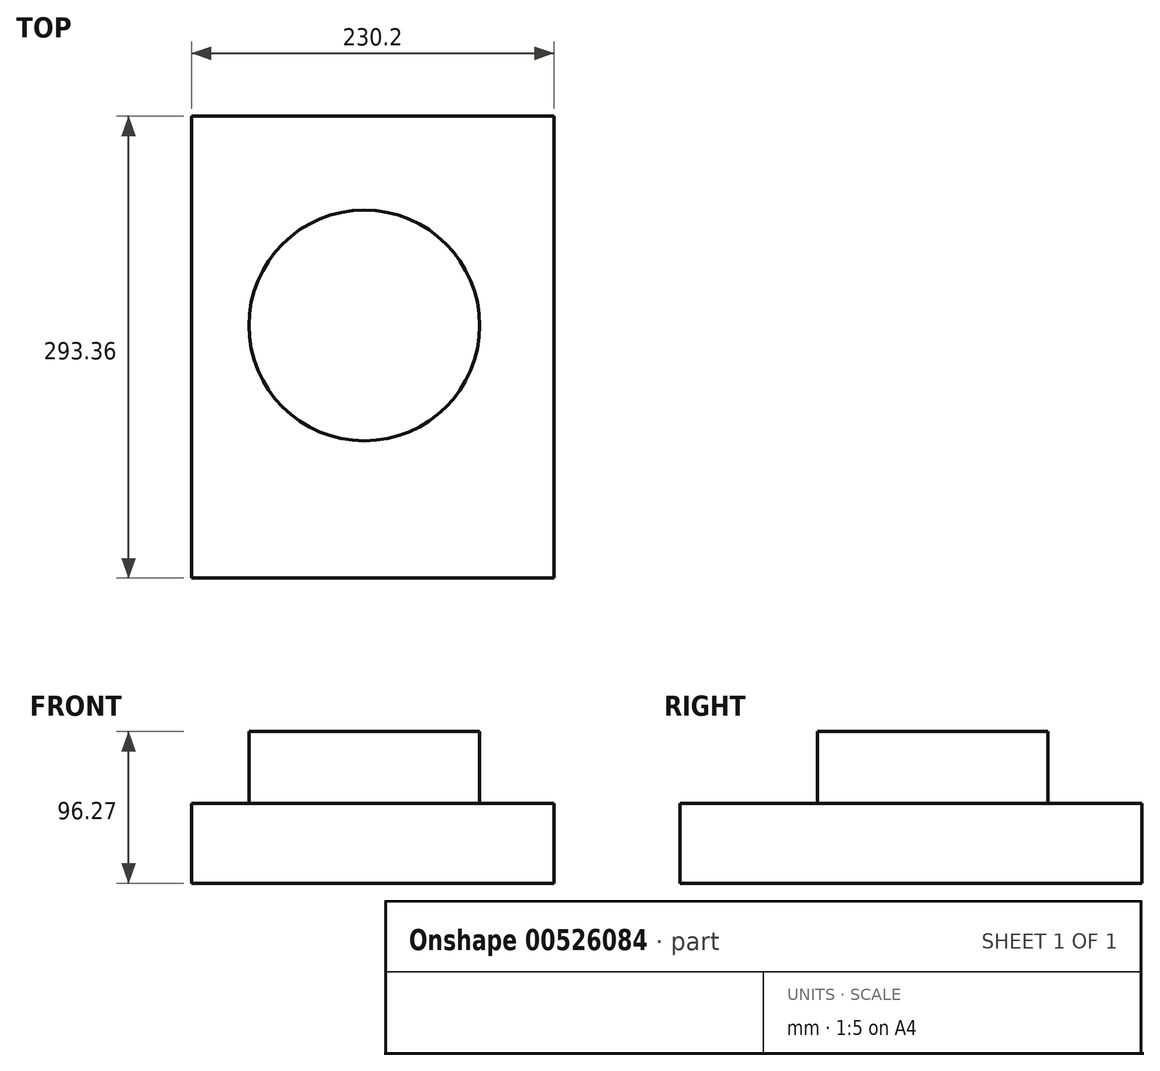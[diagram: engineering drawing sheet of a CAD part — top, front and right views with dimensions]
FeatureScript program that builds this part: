
annotation { "Feature Type Name" : "Feature", "Feature Type Description" : "" }
export const myFeature = defineFeature(function(context is Context, id is Id, definition is map)
    precondition{}
    {
        {
            var Q0;
            Q0=qCreatedBy(makeId("Top.planeOp"),FACE);
            var sketch = newSketch(context, id + "F0", { "sketchPlane" : qUnion([Q0])});
            skLineSegment(sketch, "E0.bottom", {"start": v(115.1, 146.68) * mm, "end": v(-115.1, 146.68) * mm});
            skLineSegment(sketch, "E0.top", {"start": v(115.1, -146.68) * mm, "end": v(-115.1, -146.68) * mm});
            skLineSegment(sketch, "E0.left", {"start": v(115.1, 146.68) * mm, "end": v(115.1, -146.68) * mm});
            skLineSegment(sketch, "E0.right", {"start": v(-115.1, 146.68) * mm, "end": v(-115.1, -146.68) * mm});
            skPoint(sketch, "E0.middle", {"position": v(0, 0) * mm});
            skSolve(sketch);
        }
        {
            var Q0;
            Q0=makeQuery(id+"F0.imprint","IMPRINT",FACE,{"disambiguationData":[TD([[makeQuery(id+"F0.imprint","IMPRINT",EDGE,{"derivedFrom":sQuery(id+"F0.wireOp",EDGE,"E0.bottom")}),1.0]])]});
            extrude(context, id + "F1", {"entities" : qUnion([Q0]), "depth" : 50.8 * mm, "offsetDistance" : 25.4 * mm});
        }
        {
            var Q0;
            Q0=makeQuery(id+"F1.opExtrude","CAP_FACE",FACE,{"disambiguationData":[OSD([sQuery(id+"F0.wireOp",EDGE,"E0.bottom"),sQuery(id+"F0.wireOp",EDGE,"E0.top"),sQuery(id+"F0.wireOp",EDGE,"E0.left"),sQuery(id+"F0.wireOp",EDGE,"E0.right")])],"isStart":false});
            var sketch = newSketch(context, id + "F2", { "sketchPlane" : qUnion([Q0])});
            skCircle(sketch, "E1", {"center": v(-5.39, 13.82) * mm, "radius": 73.28 * mm});
            skSolve(sketch);
        }
        {
            var Q0;
            Q0=makeQuery(id+"F2.imprint","IMPRINT",FACE,{"disambiguationData":[TD([[makeQuery(id+"F2.imprint","IMPRINT",EDGE,{"derivedFrom":sQuery(id+"F2.wireOp",EDGE,"E1")}),1.0]])]});
            extrude(context, id + "F3", {"entities" : qUnion([Q0]), "operationType" : NewBodyOperationType.ADD, "depth" : 45.47 * mm, "offsetDistance" : 25.4 * mm});
        }
    });
